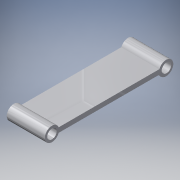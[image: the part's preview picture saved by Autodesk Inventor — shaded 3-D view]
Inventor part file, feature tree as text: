
AUTODESK INVENTOR PART (.ipt)
format: ipt  version: 2016 (Build 200138000, 138)  size: 113,664 bytes
history: native  units: in
note: dims shown in document units (in); Inventor stores cm internally (conversion verified against a paired STEP export)
features: extrude x2, sketch x2
ambient origin geometry x8: Origin, YZ Plane, XZ Plane, XY Plane, X Axis, Y Axis, Z Axis, Center Point
bodies: Solid1 (feature_tree)
feature tree (4):
  extrude  "Extrusion1"  Depth=0.125in
  extrude  "Extrusion2"  Depth=1.0in TaperAngle=0.0deg
  sketch  "Sketch1"  dims[d0=0.125in d2=0.25in]
  sketch  "Sketch2"  dims[d3=0.0625in d4=1.0in d5=0.0in d6=0.0625in d7=0.25in d8=0.0in d9=0.25in d10=1.0in d11=0.0in]
